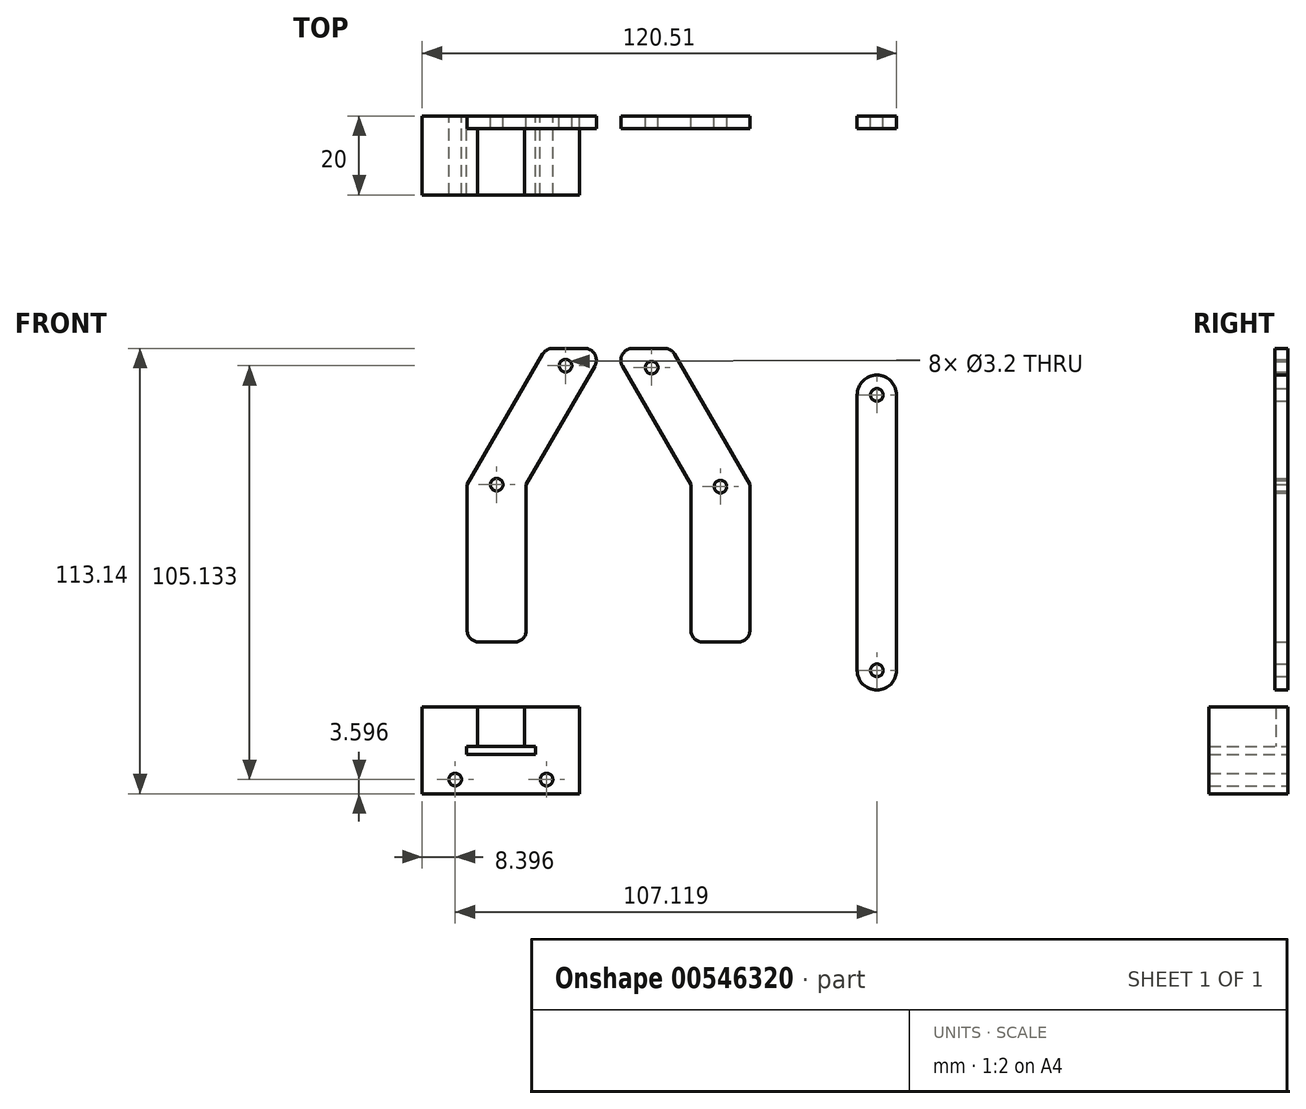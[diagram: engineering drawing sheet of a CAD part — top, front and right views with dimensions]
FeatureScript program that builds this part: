
annotation { "Feature Type Name" : "Feature", "Feature Type Description" : "" }
export const myFeature = defineFeature(function(context is Context, id is Id, definition is map)
    precondition{}
    {
        {
            var Q0;
            Q0=qCreatedBy(makeId("Front.planeOp"),FACE);
            var sketch = newSketch(context, id + "F0", { "sketchPlane" : qUnion([Q0])});
            skLineSegment(sketch, "E0", {"start": v(-51.95, 0) * mm, "end": v(-31.95, 34.64) * mm});
            skLineSegment(sketch, "E1", {"start": v(-36.95, 0) * mm, "end": v(-16.95, 34.64) * mm});
            skLineSegment(sketch, "E2", {"start": v(-51.95, 0) * mm, "end": v(-51.95, -40) * mm});
            skLineSegment(sketch, "E3", {"start": v(-51.95, -40) * mm, "end": v(-36.95, -40) * mm});
            skLineSegment(sketch, "E4", {"start": v(-36.95, -40) * mm, "end": v(-36.95, 0) * mm});
            skLineSegment(sketch, "E5", {"start": v(-0.12, 34.64) * mm, "end": v(-15.12, 34.64) * mm});
            skCircle(sketch, "E6", {"center": v(-26.97, 30.23) * mm, "radius": 1.6 * mm});
            skCircle(sketch, "E7", {"center": v(-44.45, 0) * mm, "radius": 1.6 * mm});
            skLineSegment(sketch, "E8.MirrorCS", {"start": v(4.88, 0) * mm, "end": v(-15.12, 34.64) * mm});
            skLineSegment(sketch, "E9.MirrorCS", {"start": v(19.88, 0) * mm, "end": v(-0.12, 34.64) * mm});
            skLineSegment(sketch, "E10.MirrorCS", {"start": v(4.88, -40) * mm, "end": v(4.88, 0) * mm});
            skLineSegment(sketch, "E11.MirrorCS", {"start": v(19.88, 0) * mm, "end": v(19.88, -40) * mm});
            skLineSegment(sketch, "E12.MirrorCS", {"start": v(19.88, -40) * mm, "end": v(4.88, -40) * mm});
            skCircle(sketch, "E13.MirrorC", {"center": v(12.38, -0.48) * mm, "radius": 1.6 * mm});
            skCircle(sketch, "E14.MirrorC", {"center": v(-5.1, 29.75) * mm, "radius": 1.6 * mm});
            skLineSegment(sketch, "E15", {"start": v(-31.95, 34.64) * mm, "end": v(-16.95, 34.64) * mm});
            skSolve(sketch);
        }
        {
            var Q0;
            Q0=makeQuery(id+"F0.imprint","IMPRINT",FACE,{"disambiguationData":[TD([[makeQuery(id+"F0.imprint","IMPRINT",EDGE,{"derivedFrom":sQuery(id+"F0.wireOp",EDGE,"E5")}),1.0]])]});
            var Q1;
            Q1=makeQuery(id+"F0.imprint","IMPRINT",FACE,{"disambiguationData":[TD([[makeQuery(id+"F0.imprint","IMPRINT",EDGE,{"derivedFrom":sQuery(id+"F0.wireOp",EDGE,"E0")}),-1.0]])]});
            extrude(context, id + "F1", {"entities" : qUnion([Q0, Q1]), "depth" : 3.2 * mm, "offsetDistance" : 25 * mm});
        }
        {
            var Q0;
            Q0=makeQuery(id+"F1.opExtrude","SWEPT_EDGE",EDGE,{"disambiguationData":[OSD([sQuery(id+"F0.wireOp",EDGE,"E2"),sQuery(id+"F0.wireOp",EDGE,"E3")])]});
            var Q1;
            Q1=makeQuery(id+"F1.opExtrude","SWEPT_EDGE",EDGE,{"disambiguationData":[OSD([sQuery(id+"F0.wireOp",EDGE,"E3"),sQuery(id+"F0.wireOp",EDGE,"E4")])]});
            var Q2;
            Q2=makeQuery(id+"F1.opExtrude","SWEPT_EDGE",EDGE,{"disambiguationData":[OSD([sQuery(id+"F0.wireOp",EDGE,"E11.MirrorCS"),sQuery(id+"F0.wireOp",EDGE,"E12.MirrorCS")])]});
            var Q3;
            Q3=makeQuery(id+"F1.opExtrude","SWEPT_EDGE",EDGE,{"disambiguationData":[OSD([sQuery(id+"F0.wireOp",EDGE,"E10.MirrorCS"),sQuery(id+"F0.wireOp",EDGE,"E12.MirrorCS")])]});
            var Q4;
            Q4=makeQuery(id+"F1.opExtrude","SWEPT_EDGE",EDGE,{"disambiguationData":[OSD([sQuery(id+"F0.wireOp",EDGE,"E0"),sQuery(id+"F0.wireOp",EDGE,"E15")])]});
            var Q5;
            Q5=makeQuery(id+"F1.opExtrude","SWEPT_EDGE",EDGE,{"disambiguationData":[OSD([sQuery(id+"F0.wireOp",EDGE,"E1"),sQuery(id+"F0.wireOp",EDGE,"E15")])]});
            var Q6;
            Q6=makeQuery(id+"F1.opExtrude","SWEPT_EDGE",EDGE,{"disambiguationData":[OSD([sQuery(id+"F0.wireOp",EDGE,"E5"),sQuery(id+"F0.wireOp",EDGE,"E8.MirrorCS")])]});
            var Q7;
            Q7=makeQuery(id+"F1.opExtrude","SWEPT_EDGE",EDGE,{"disambiguationData":[OSD([sQuery(id+"F0.wireOp",EDGE,"E5"),sQuery(id+"F0.wireOp",EDGE,"E9.MirrorCS")])]});
            fillet(context, id + "F2", {"entities" : qUnion([Q0, Q1, Q2, Q3, Q4, Q5, Q6, Q7]), "radius" : 3 * mm, "tangentPropagation" : true, "allowEdgeOverflow" : false});
        }
        {
            var Q0;
            Q0=qCreatedBy(makeId("Front.planeOp"),FACE);
            var sketch = newSketch(context, id + "F3", { "sketchPlane" : qUnion([Q0])});
            skLineSegment(sketch, "E16.bottom", {"start": v(47.12, 22.83) * mm, "end": v(57.12, 22.83) * mm});
            skLineSegment(sketch, "E16.top", {"start": v(47.12, -47.17) * mm, "end": v(57.12, -47.17) * mm});
            skLineSegment(sketch, "E16.left", {"start": v(47.12, 22.83) * mm, "end": v(47.12, -47.17) * mm});
            skLineSegment(sketch, "E16.right", {"start": v(57.12, 22.83) * mm, "end": v(57.12, -47.17) * mm});
            skCircle(sketch, "E17", {"center": v(52.12, 22.83) * mm, "radius": 5 * mm});
            skCircle(sketch, "E18", {"center": v(52.12, -47.17) * mm, "radius": 5 * mm});
            skCircle(sketch, "E19", {"center": v(52.12, 22.83) * mm, "radius": 1.6 * mm});
            skCircle(sketch, "E20", {"center": v(52.12, -47.17) * mm, "radius": 1.6 * mm});
            skSolve(sketch);
        }
        {
            var Q0;
            Q0=qSketchRegion(id+"F3",true);
            extrude(context, id + "F4", {"entities" : qUnion([Q0]), "depth" : 3.2 * mm, "offsetDistance" : 25 * mm});
        }
        {
            var Q0;
            Q0=qCreatedBy(makeId("Front.planeOp"),FACE);
            var sketch = newSketch(context, id + "F5", { "sketchPlane" : qUnion([Q0])});
            skLineSegment(sketch, "E21.bottom", {"start": v(-63.4, -56.5) * mm, "end": v(-23.4, -56.5) * mm});
            skLineSegment(sketch, "E21.top", {"start": v(-63.4, -78.5) * mm, "end": v(-23.4, -78.5) * mm});
            skLineSegment(sketch, "E21.left", {"start": v(-63.4, -56.5) * mm, "end": v(-63.4, -78.5) * mm});
            skLineSegment(sketch, "E21.right", {"start": v(-23.4, -56.5) * mm, "end": v(-23.4, -78.5) * mm});
            skLineSegment(sketch, "E22", {"start": v(-49.4, -56.5) * mm, "end": v(-49.4, -66.5) * mm});
            skLineSegment(sketch, "E23", {"start": v(-37.4, -56.5) * mm, "end": v(-37.4, -66.5) * mm});
            skLineSegment(sketch, "E24", {"start": v(-49.4, -56.5) * mm, "end": v(-37.4, -56.5) * mm});
            skLineSegment(sketch, "E25", {"start": v(-37.4, -56.5) * mm, "end": v(-49.4, -56.5) * mm});
            skLineSegment(sketch, "E26.bottom", {"start": v(-52.14, -66.5) * mm, "end": v(-34.64, -66.5) * mm});
            skLineSegment(sketch, "E26.top", {"start": v(-52.14, -68.5) * mm, "end": v(-34.64, -68.5) * mm});
            skLineSegment(sketch, "E26.left", {"start": v(-52.14, -66.5) * mm, "end": v(-52.14, -68.5) * mm});
            skLineSegment(sketch, "E26.right", {"start": v(-34.64, -66.5) * mm, "end": v(-34.64, -68.5) * mm});
            skCircle(sketch, "E27", {"center": v(-55, -74.9) * mm, "radius": 1.6 * mm});
            skCircle(sketch, "E28", {"center": v(-31.8, -74.9) * mm, "radius": 1.6 * mm});
            skSolve(sketch);
        }
        {
            var Q0;
            Q0=makeQuery(id+"F5.imprint","IMPRINT",FACE,{"disambiguationData":[TD([[makeQuery(id+"F5.imprint","IMPRINT",EDGE,{"derivedFrom":sQuery(id+"F5.wireOp",EDGE,"E21.top")}),1.0]])]});
            extrude(context, id + "F6", {"entities" : qUnion([Q0]), "depth" : 20 * mm, "offsetDistance" : 25 * mm});
        }
        {
            var Q0;
            {var subQ0=sQuery(id+"F5.wireOp",EDGE,"E22");Q0=makeQuery(id+"F5.imprint","IMPRINT",FACE,{"disambiguationData":[TD([[makeQuery(id+"F5.imprint","IMPRINT",EDGE,{"derivedFrom":subQ0}),1.0]])]});}
            extrude(context, id + "F7", {"entities" : qUnion([Q0]), "operationType" : NewBodyOperationType.ADD, "depth" : 3 * mm, "offsetDistance" : 25 * mm});
        }
    });
